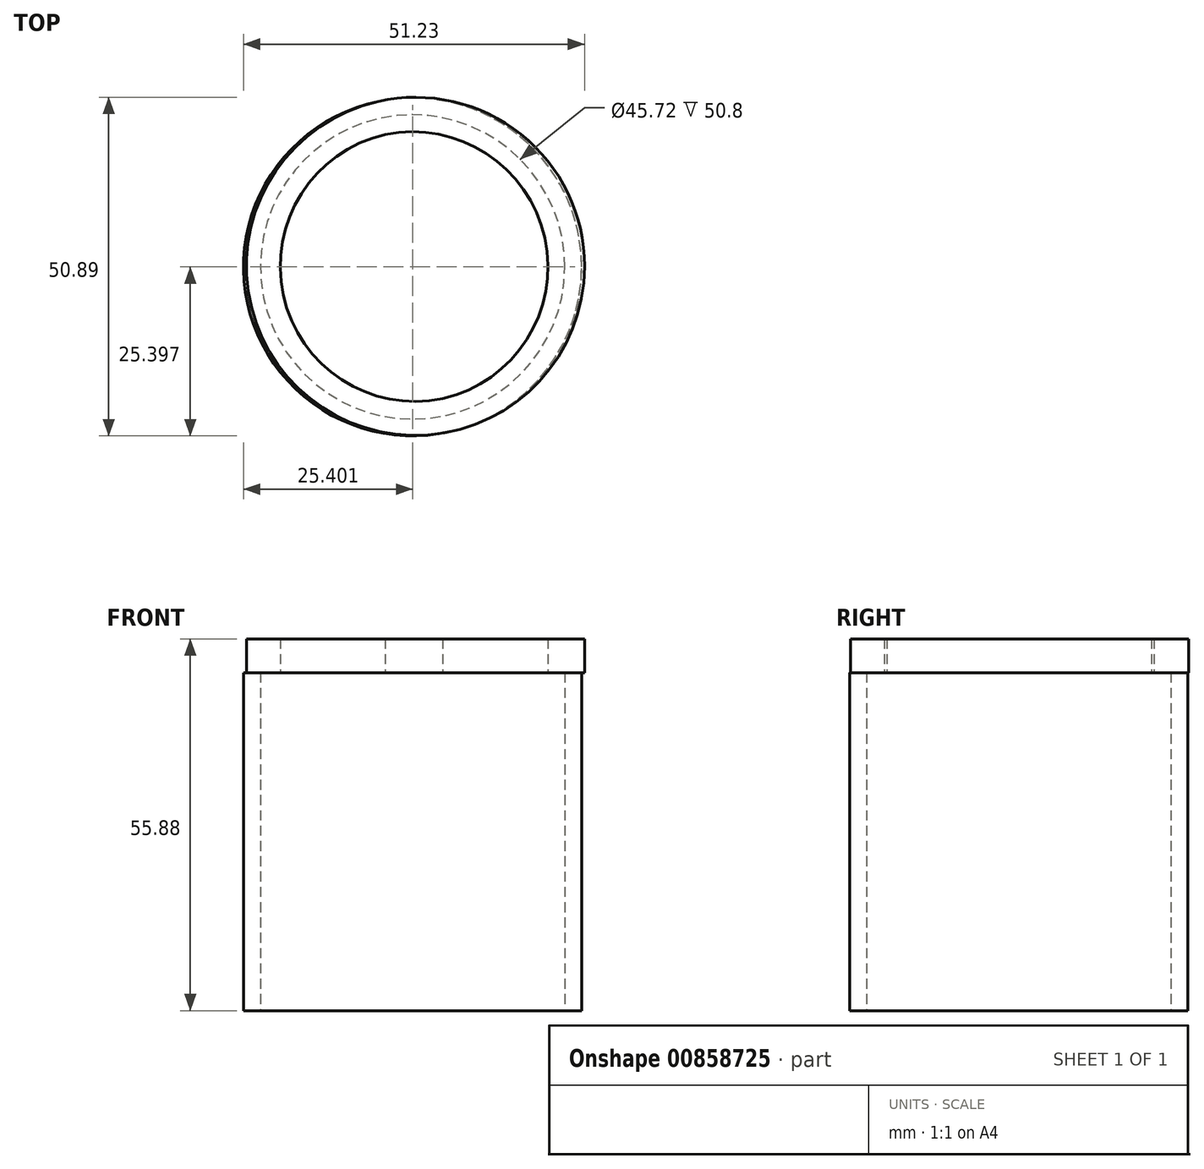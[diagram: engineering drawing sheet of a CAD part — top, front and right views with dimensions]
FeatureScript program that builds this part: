
annotation { "Feature Type Name" : "Feature", "Feature Type Description" : "" }
export const myFeature = defineFeature(function(context is Context, id is Id, definition is map)
    precondition{}
    {
        {
            var Q0;
            Q0=qCreatedBy(makeId("Top.planeOp"),FACE);
            var sketch = newSketch(context, id + "F0", { "sketchPlane" : qUnion([Q0])});
            skCircle(sketch, "E0", {"center": v(-0.43, -0.1) * mm, "radius": 25.4 * mm});
            skPoint(sketch, "E0.first.point", {"position": v(-20.1, 15.96) * mm});
            skPoint(sketch, "E0.second.point", {"position": v(15.19, -20.13) * mm});
            skPoint(sketch, "E0.third.point", {"position": v(17.3, 18.09) * mm});
            skPoint(sketch, "E1", {"position": v(0, 0) * mm});
            skPoint(sketch, "E2", {"position": v(-0.43, 25.3) * mm});
            skPoint(sketch, "E3", {"position": v(0, -25.49) * mm});
            skPoint(sketch, "E4", {"position": v(-25.83, -0.1) * mm});
            skPoint(sketch, "E5", {"position": v(24.97, -0.1) * mm});
            skSolve(sketch);
        }
        {
            var Q0;
            Q0=makeQuery(id+"F0.imprint","IMPRINT",FACE,{"disambiguationData":[TD([[makeQuery(id+"F0.imprint","IMPRINT",EDGE,{"derivedFrom":sQuery(id+"F0.wireOp",EDGE,"E0")}),1.0]])]});
            extrude(context, id + "F1", {"entities" : qUnion([Q0]), "depth" : 50.8 * mm, "offsetDistance" : 25.4 * mm});
        }
        {
            var Q0;
            Q0=makeQuery(id+"F1.opExtrude","CAP_FACE",FACE,{"disambiguationData":[OSD([sQuery(id+"F0.wireOp",EDGE,"E0")])],"isStart":false});
            var Q1;
            Q1=makeQuery(id+"F1.opExtrude","CAP_FACE",FACE,{"disambiguationData":[OSD([sQuery(id+"F0.wireOp",EDGE,"E0")])],"isStart":true});
            shell(context, id + "F2", {"entities" : qUnion([Q0, Q1]), "thickness" : 2.54 * mm});
        }
        {
            var Q0;
            Q0=makeQuery(id+"F1.opExtrude","CAP_FACE",FACE,{"disambiguationData":[OSD([sQuery(id+"F0.wireOp",EDGE,"E0")])],"isStart":false});
            var sketch = newSketch(context, id + "F3", { "sketchPlane" : qUnion([Q0])});
            skCircle(sketch, "E6", {"center": v(0, 0) * mm, "radius": 25.4 * mm});
            skSolve(sketch);
        }
        {
            var Q0;
            Q0 = qSketchRegion(id + "F3", true);
            extrude(context, id + "F4", {"entities" : qUnion([Q0]), "operationType" : NewBodyOperationType.ADD, "depth" : 5.08 * mm, "offsetDistance" : 25.4 * mm});
        }
        {
            var Q0;
            Q0=makeQuery(id+"F4.opExtrude","CAP_FACE",FACE,{"disambiguationData":[OSD([sQuery(id+"F3.wireOp",EDGE,"E6")])],"isStart":false});
            var Q1;
            Q1=makeQuery(id+"F4.boolean.opBoolean","SPLIT",FACE,{"disambiguationData":[TD([makeQuery(id+"F2.opShell","OFFSET_FACE",FACE,{"disambiguationData":[OSD([sQuery(id+"F0.wireOp",EDGE,"E0")])]})])],"derivedFrom":makeQuery(id+"F4.opExtrude","CAP_FACE",FACE,{"disambiguationData":[OSD([sQuery(id+"F3.wireOp",EDGE,"E6")])],"isStart":true})});
            shell(context, id + "F5", {"entities" : qUnion([Q0, Q1]), "thickness" : 5.08 * mm});
        }
    });
